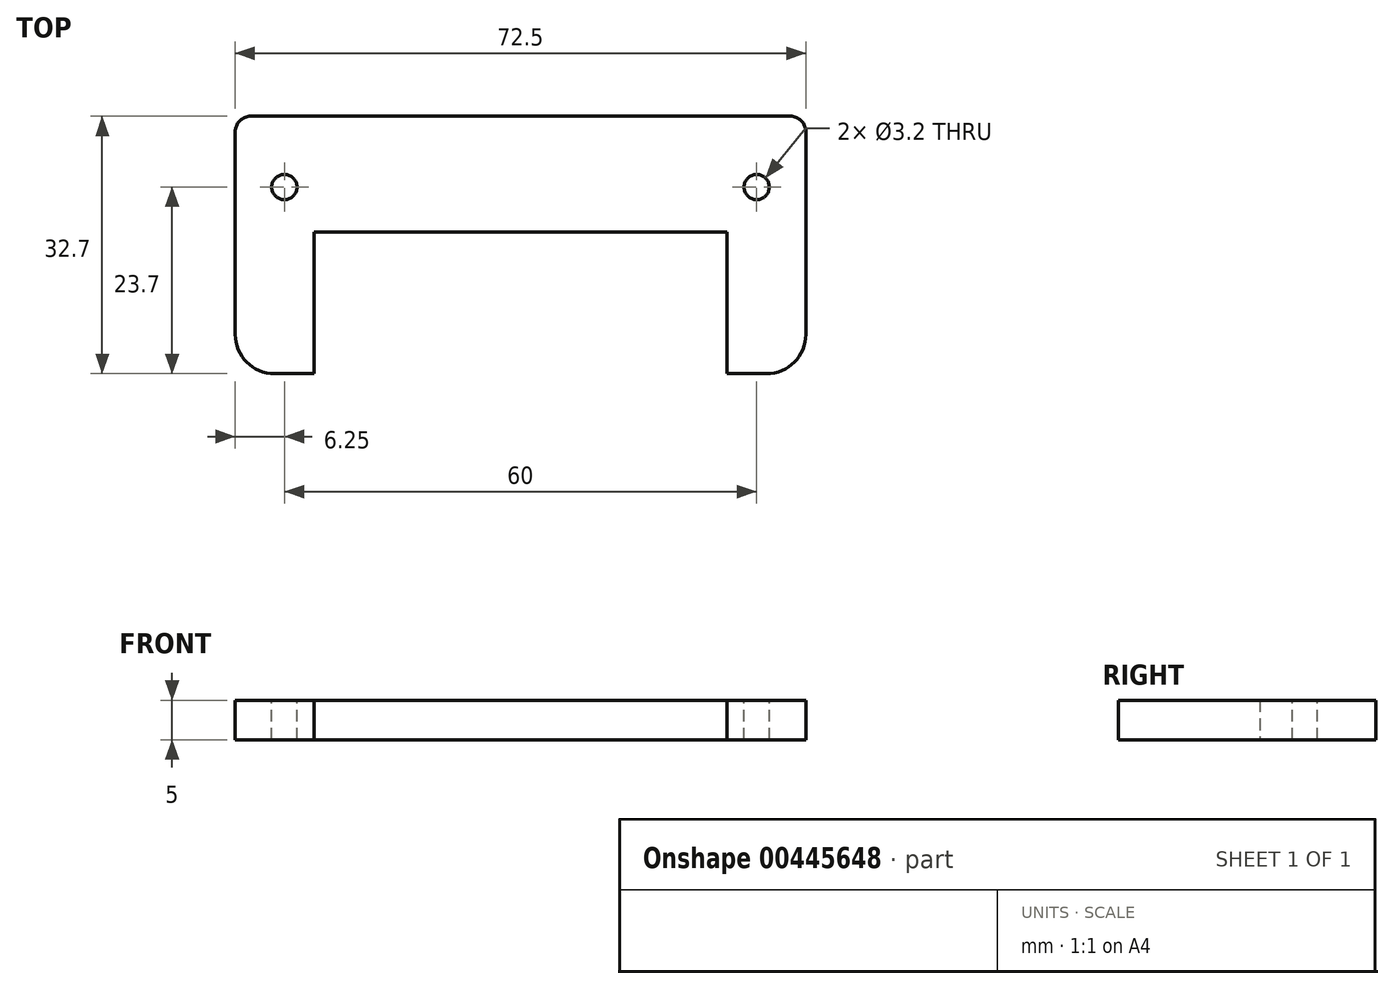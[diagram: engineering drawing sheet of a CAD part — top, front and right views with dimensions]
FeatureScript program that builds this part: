
annotation { "Feature Type Name" : "Feature", "Feature Type Description" : "" }
export const myFeature = defineFeature(function(context is Context, id is Id, definition is map)
    precondition{}
    {
        {
            var Q0;
            Q0=qCreatedBy(makeId("Top.planeOp"),FACE);
            var sketch = newSketch(context, id + "F0", { "sketchPlane" : qUnion([Q0])});
            skLineSegment(sketch, "E0.bottom", {"start": v(-36.25, -16.35) * mm, "end": v(-26.25, -16.35) * mm});
            skLineSegment(sketch, "E0.top", {"start": v(-36.25, 16.35) * mm, "end": v(36.25, 16.35) * mm});
            skLineSegment(sketch, "E0.left", {"start": v(-36.25, -16.35) * mm, "end": v(-36.25, 16.35) * mm});
            skLineSegment(sketch, "E0.right", {"start": v(36.25, -16.35) * mm, "end": v(36.25, 16.35) * mm});
            skPoint(sketch, "E0.middle", {"position": v(0, 0) * mm});
            skLineSegment(sketch, "E1.top", {"start": v(-26.25, 1.65) * mm, "end": v(26.25, 1.65) * mm});
            skLineSegment(sketch, "E1.left", {"start": v(-26.25, -16.35) * mm, "end": v(-26.25, 1.65) * mm});
            skLineSegment(sketch, "E1.right", {"start": v(26.25, -16.35) * mm, "end": v(26.25, 1.65) * mm});
            skLineSegment(sketch, "E2.trimOffspring", {"start": v(26.25, -16.35) * mm, "end": v(36.25, -16.35) * mm});
            skSolve(sketch);
        }
        {
            var Q0;
            Q0=qSketchRegion(id+"F0",true);
            extrude(context, id + "F1", {"entities" : qUnion([Q0]), "depth" : 5 * mm});
        }
        {
            var Q0;
            Q0=makeQuery(id+"F1.opExtrude","CAP_FACE",FACE,{"disambiguationData":[OSD([sQuery(id+"F0.wireOp",EDGE,"E0.bottom"),sQuery(id+"F0.wireOp",EDGE,"E0.top"),sQuery(id+"F0.wireOp",EDGE,"E0.left"),sQuery(id+"F0.wireOp",EDGE,"E0.right"),sQuery(id+"F0.wireOp",EDGE,"E1.top"),sQuery(id+"F0.wireOp",EDGE,"E1.left"),sQuery(id+"F0.wireOp",EDGE,"E1.right"),sQuery(id+"F0.wireOp",EDGE,"E2.trimOffspring")])],"isStart":false});
            var sketch = newSketch(context, id + "F2", { "sketchPlane" : qUnion([Q0])});
            skPoint(sketch, "E3", {"position": v(-30, 7.35) * mm});
            skPoint(sketch, "E4.1.0.0", {"position": v(30, 7.35) * mm});
            skLineSegment(sketch, "E4.direction1", {"start": v(-30, 7.35) * mm, "end": v(30, 7.35) * mm, "construction": true});
            skSolve(sketch);
        }
        {
            var Q0;
            Q0=sQuery(id+"F2.wireOp",VERTEX,"E3");
            var Q1;
            Q1=sQuery(id+"F2.wireOp",VERTEX,"E4.1.0.0");
            var Q2;
            Q2=makeQuery(id+"F1.opExtrude","SWEPT_BODY",BODY,{"disambiguationData":[OSD([sQuery(id+"F0.wireOp",EDGE,"E0.bottom"),sQuery(id+"F0.wireOp",EDGE,"E0.top"),sQuery(id+"F0.wireOp",EDGE,"E0.left"),sQuery(id+"F0.wireOp",EDGE,"E0.right"),sQuery(id+"F0.wireOp",EDGE,"E1.top"),sQuery(id+"F0.wireOp",EDGE,"E1.left"),sQuery(id+"F0.wireOp",EDGE,"E1.right"),sQuery(id+"F0.wireOp",EDGE,"E2.trimOffspring")])]});
            hole(context, id + "F3", {"style" : HoleStyle.SIMPLE, "endStyle" : HoleEndStyle.BLIND, "standardTappedOrClearance" : lookupTablePath({ "standard" : "ISO", "engagement" : "75%", "pitch" : "0.75 mm", "size" : "M4", "type" : "Tapped" }), "standardBlindInLast" : lookupTablePath({ "standard" : "ISO", "engagement" : "75%", "pitch" : "0.75 mm", "size" : "M4", "type" : "Tapped" }), "holeDiameter" : 3.2 * mm, "showTappedDepth" : true, "holeDepth" : 14.25 * mm, "tappedDepth" : 12 * mm, "tapClearance" : 3, "locations" : qUnion([Q0, Q1]), "scope" : qUnion([Q2])});
        }
        {
            var Q0;
            Q0=makeQuery(id+"F1.opExtrude","SWEPT_EDGE",EDGE,{"disambiguationData":[OSD([sQuery(id+"F0.wireOp",EDGE,"E0.bottom"),sQuery(id+"F0.wireOp",EDGE,"E0.left")])]});
            var Q1;
            Q1=makeQuery(id+"F1.opExtrude","SWEPT_EDGE",EDGE,{"disambiguationData":[OSD([sQuery(id+"F0.wireOp",EDGE,"E0.right"),sQuery(id+"F0.wireOp",EDGE,"E2.trimOffspring")])]});
            fillet(context, id + "F4", {"entities" : qUnion([Q0, Q1]), "radius" : 5 * mm, "tangentPropagation" : true, "allowEdgeOverflow" : false});
        }
        {
            var Q0;
            Q0=makeQuery(id+"F1.opExtrude","SWEPT_EDGE",EDGE,{"disambiguationData":[OSD([sQuery(id+"F0.wireOp",EDGE,"E0.top"),sQuery(id+"F0.wireOp",EDGE,"E0.right")])]});
            var Q1;
            Q1=makeQuery(id+"F1.opExtrude","SWEPT_EDGE",EDGE,{"disambiguationData":[OSD([sQuery(id+"F0.wireOp",EDGE,"E0.top"),sQuery(id+"F0.wireOp",EDGE,"E0.left")])]});
            fillet(context, id + "F5", {"entities" : qUnion([Q0, Q1]), "radius" : 2 * mm, "tangentPropagation" : true, "allowEdgeOverflow" : false});
        }
    });
